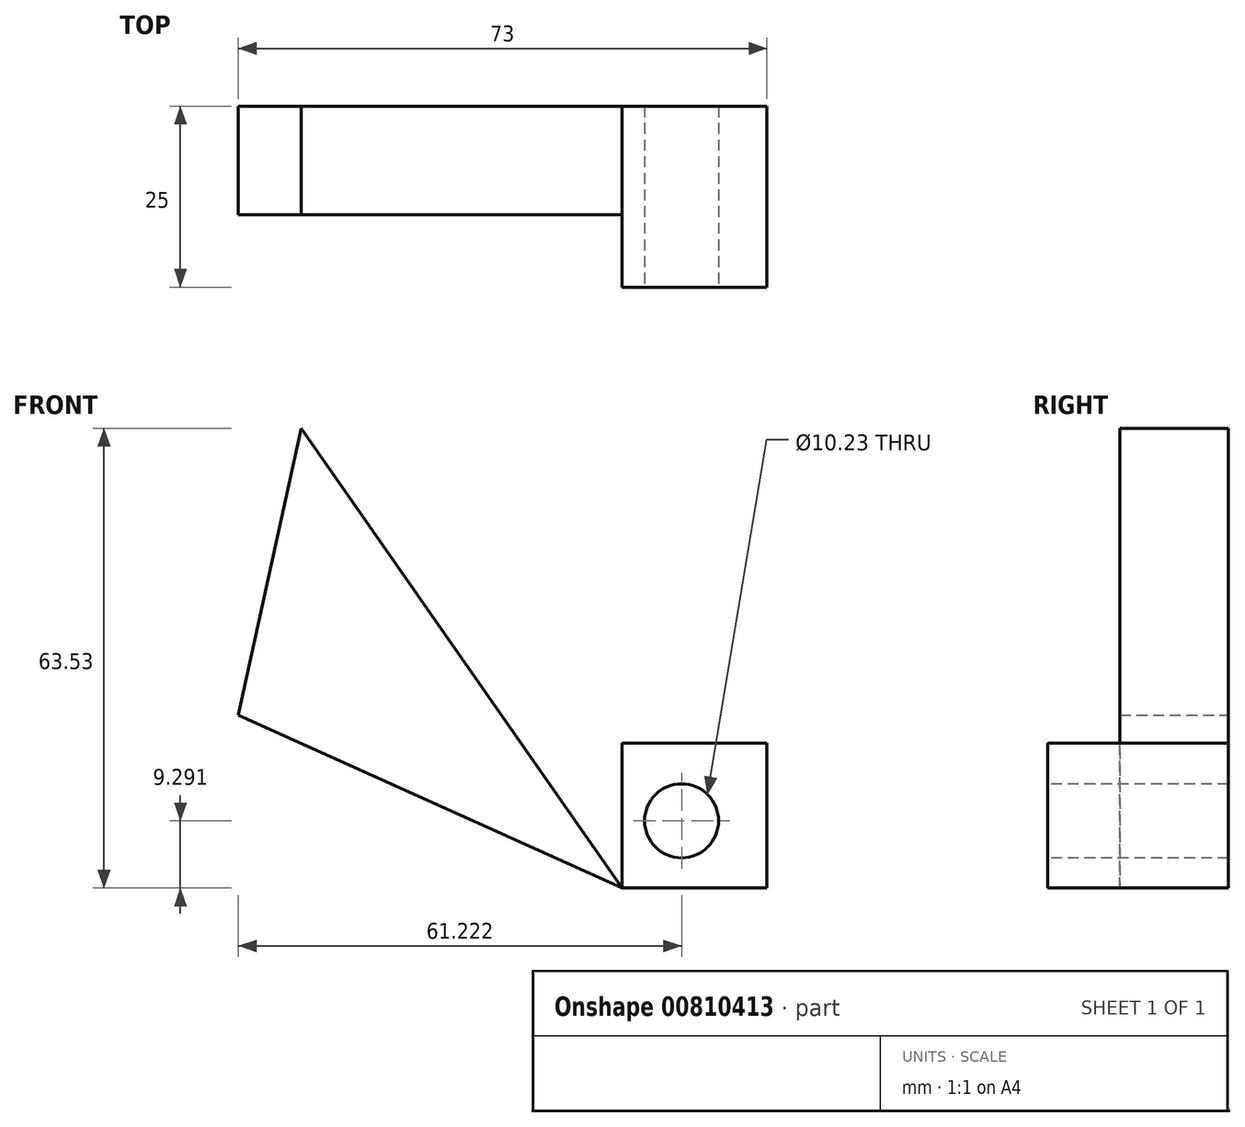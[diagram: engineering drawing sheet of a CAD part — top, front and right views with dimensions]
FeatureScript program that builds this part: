
annotation { "Feature Type Name" : "Feature", "Feature Type Description" : "" }
export const myFeature = defineFeature(function(context is Context, id is Id, definition is map)
    precondition{}
    {
        {
            var Q0;
            Q0=qCreatedBy(makeId("Front.planeOp"),FACE);
            var sketch = newSketch(context, id + "F0", { "sketchPlane" : qUnion([Q0])});
            skLineSegment(sketch, "E0", {"start": v(0, 0) * mm, "end": v(-44.3, 63.53) * mm});
            skLineSegment(sketch, "E1", {"start": v(-44.3, 63.53) * mm, "end": v(-53, 23.92) * mm});
            skLineSegment(sketch, "E2", {"start": v(-53, 23.92) * mm, "end": v(0, 0) * mm});
            skSolve(sketch);
        }
        {
            var Q0;
            Q0 = qSketchRegion(id + "F0", true);
            extrude(context, id + "F1", {"entities" : qUnion([Q0]), "depth" : 15 * mm, "offsetDistance" : 25 * mm});
        }
        {
            var Q0;
            Q0=qCreatedBy(makeId("Front.planeOp"),FACE);
            var sketch = newSketch(context, id + "F2", { "sketchPlane" : qUnion([Q0])});
            skLineSegment(sketch, "E3", {"start": v(0, 0) * mm, "end": v(0, 20) * mm});
            skLineSegment(sketch, "E4", {"start": v(0, 20) * mm, "end": v(20, 20) * mm});
            skLineSegment(sketch, "E5", {"start": v(20, 20) * mm, "end": v(20, 0) * mm});
            skLineSegment(sketch, "E6", {"start": v(20, 0) * mm, "end": v(0, 0) * mm});
            skSolve(sketch);
        }
        {
            var Q0;
            Q0 = qSketchRegion(id + "F2", true);
            extrude(context, id + "F3", {"entities" : qUnion([Q0]), "depth" : 20 * mm, "offsetDistance" : 25 * mm});
        }
        {
            var Q0;
            Q0=makeQuery(id+"F3.opExtrude","CAP_FACE",FACE,{"disambiguationData":[OSD([sQuery(id+"F2.wireOp",EDGE,"E3"),sQuery(id+"F2.wireOp",EDGE,"E4"),sQuery(id+"F2.wireOp",EDGE,"E5"),sQuery(id+"F2.wireOp",EDGE,"E6")])],"isStart":true});
            var sketch = newSketch(context, id + "F4", { "sketchPlane" : qUnion([Q0])});
            skSolve(sketch);
        }
        {
            var Q0;
            Q0=makeQuery(id+"F3.opExtrude","CAP_FACE",FACE,{"disambiguationData":[OSD([sQuery(id+"F2.wireOp",EDGE,"E3"),sQuery(id+"F2.wireOp",EDGE,"E4"),sQuery(id+"F2.wireOp",EDGE,"E5"),sQuery(id+"F2.wireOp",EDGE,"E6")])],"isStart":true});
            var sketch = newSketch(context, id + "F5", { "sketchPlane" : qUnion([Q0])});
            skCircle(sketch, "E7", {"center": v(-11.18, 10) * mm, "radius": 7.57 * mm});
            skPoint(sketch, "E7.centerSnap0", {"position": v(-20, 10) * mm});
            skSolve(sketch);
        }
        {
            var Q0;
            Q0 = qSketchRegion(id + "F5", true);
            var Q1;
            Q1=makeQuery(id+"F4.imprint","IMPRINT",FACE,{"disambiguationData":[TD([[makeQuery(id+"F4.imprint","IMPRINT",EDGE,{"derivedFrom":makeQuery(id+"F3.opExtrude","CAP_EDGE",EDGE,{"disambiguationData":[OSD([sQuery(id+"F2.wireOp",EDGE,"E3")])],"isStart":true})}),1.0]])]});
            extrude(context, id + "F6", {"entities" : qUnion([Q0, Q1]), "operationType" : NewBodyOperationType.ADD, "depth" : -25 * mm, "offsetDistance" : 25 * mm});
        }
        {
            var Q0;
            Q0=makeQuery(id+"F6.opExtrude","CAP_FACE",FACE,{"disambiguationData":[OSD([sQuery(id+"F2.wireOp",EDGE,"E3"),sQuery(id+"F2.wireOp",EDGE,"E4"),sQuery(id+"F2.wireOp",EDGE,"E5"),sQuery(id+"F2.wireOp",EDGE,"E6")])],"isStart":false});
            var sketch = newSketch(context, id + "F7", { "sketchPlane" : qUnion([Q0])});
            skCircle(sketch, "E8", {"center": v(8.22, 9.3) * mm, "radius": 5.12 * mm});
            skSolve(sketch);
        }
        {
            var Q0;
            Q0=makeQuery(id+"F7.imprint","IMPRINT",FACE,{"disambiguationData":[TD([[makeQuery(id+"F7.imprint","IMPRINT",EDGE,{"derivedFrom":sQuery(id+"F7.wireOp",EDGE,"E8")}),1.0]])]});
            extrude(context, id + "F8", {"entities" : qUnion([Q0]), "operationType" : NewBodyOperationType.REMOVE, "oppositeDirection" : true, "depth" : 25 * mm, "offsetDistance" : 25 * mm});
        }
    });
